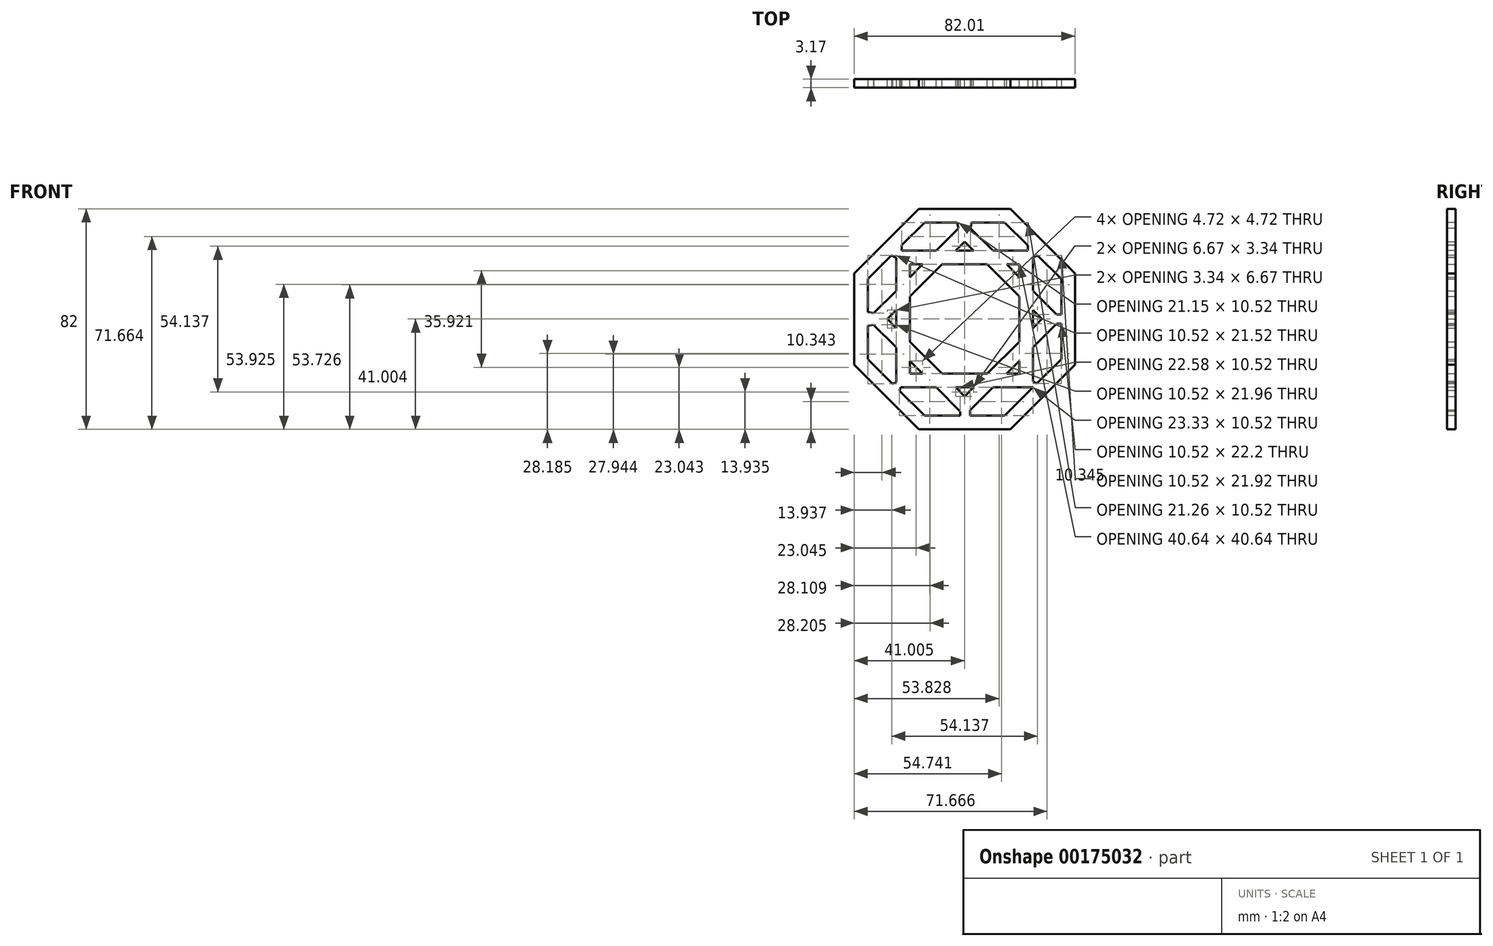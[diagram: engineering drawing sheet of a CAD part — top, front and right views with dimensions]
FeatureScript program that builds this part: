
annotation { "Feature Type Name" : "Feature", "Feature Type Description" : "" }
export const myFeature = defineFeature(function(context is Context, id is Id, definition is map)
    precondition{}
    {
        {
            var Q0;
            Q0=qCreatedBy(makeId("Front.planeOp"),FACE);
            var sketch = newSketch(context, id + "F0", { "sketchPlane" : qUnion([Q0])});
            skLineSegment(sketch, "E0.bottom", {"start": v(2.39, 24.41) * mm, "end": v(53.19, 24.41) * mm});
            skLineSegment(sketch, "E0.top", {"start": v(2.39, -26.39) * mm, "end": v(53.19, -26.39) * mm});
            skLineSegment(sketch, "E0.left", {"start": v(2.39, 24.41) * mm, "end": v(2.39, -26.39) * mm});
            skLineSegment(sketch, "E0.right", {"start": v(53.19, 24.41) * mm, "end": v(53.19, -26.39) * mm});
            skLineSegment(sketch, "E1.bottom", {"start": v(7.47, 19.33) * mm, "end": v(48.1, 19.33) * mm});
            skLineSegment(sketch, "E1.top", {"start": v(7.47, -21.3) * mm, "end": v(48.1, -21.3) * mm});
            skLineSegment(sketch, "E1.left", {"start": v(7.47, 19.33) * mm, "end": v(7.47, -21.3) * mm});
            skLineSegment(sketch, "E1.right", {"start": v(48.1, 19.33) * mm, "end": v(48.1, -21.3) * mm});
            skLineSegment(sketch, "E2.0", {"start": v(63.7, -0.99) * mm, "end": v(27.79, -36.9) * mm});
            skLineSegment(sketch, "E2.1", {"start": v(27.79, -36.9) * mm, "end": v(-8.14, -0.99) * mm});
            skLineSegment(sketch, "E2.2", {"start": v(-8.14, -0.99) * mm, "end": v(27.79, 34.93) * mm});
            skLineSegment(sketch, "E2.3", {"start": v(27.79, 34.93) * mm, "end": v(63.7, -0.99) * mm});
            skPoint(sketch, "E2.0.midPoint", {"position": v(45.75, -18.95) * mm});
            skPoint(sketch, "E3.0.midPoint", {"position": v(2.39, -0.99) * mm});
            skLineSegment(sketch, "E4.0", {"start": v(56.52, -0.99) * mm, "end": v(27.79, -29.72) * mm});
            skLineSegment(sketch, "E4.1", {"start": v(27.79, -29.72) * mm, "end": v(-0.95, -0.99) * mm});
            skLineSegment(sketch, "E4.2", {"start": v(-0.95, -0.99) * mm, "end": v(27.79, 27.75) * mm});
            skLineSegment(sketch, "E4.3", {"start": v(27.79, 27.75) * mm, "end": v(56.52, -0.99) * mm});
            skPoint(sketch, "E4.0.midPoint", {"position": v(42.15, -15.35) * mm});
            skPoint(sketch, "E5", {"position": v(48.1, -0.99) * mm});
            skPoint(sketch, "E6", {"position": v(27.79, 24.41) * mm});
            skPoint(sketch, "E7", {"position": v(53.19, -0.99) * mm});
            skCircle(sketch, "E8.cCircle", {"center": v(27.79, -0.99) * mm, "radius": 41 * mm, "construction": true});
            skLineSegment(sketch, "E8.0", {"start": v(-13.22, 16) * mm, "end": v(10.8, 40.01) * mm});
            skLineSegment(sketch, "E8.1", {"start": v(10.8, 40.01) * mm, "end": v(44.77, 40.01) * mm});
            skLineSegment(sketch, "E8.2", {"start": v(44.77, 40.01) * mm, "end": v(68.79, 16) * mm});
            skLineSegment(sketch, "E8.3", {"start": v(68.79, 16) * mm, "end": v(68.79, -17.97) * mm});
            skLineSegment(sketch, "E8.4", {"start": v(68.79, -17.97) * mm, "end": v(44.77, -41.99) * mm});
            skLineSegment(sketch, "E8.5", {"start": v(44.77, -41.99) * mm, "end": v(10.8, -41.99) * mm});
            skLineSegment(sketch, "E8.6", {"start": v(10.8, -41.99) * mm, "end": v(-13.22, -17.97) * mm});
            skLineSegment(sketch, "E8.7", {"start": v(-13.22, -17.97) * mm, "end": v(-13.22, 16) * mm});
            skPoint(sketch, "E8.0.midPoint", {"position": v(-1.2, 28) * mm});
            skPoint(sketch, "E9", {"position": v(-13.22, -0.99) * mm});
            skPoint(sketch, "E10", {"position": v(68.79, -0.99) * mm});
            skPoint(sketch, "E11", {"position": v(27.79, 40.01) * mm});
            skPoint(sketch, "E12", {"position": v(27.79, -41.99) * mm});
            skCircle(sketch, "E13.cCircle", {"center": v(27.79, -0.99) * mm, "radius": 35.92 * mm, "construction": true});
            skLineSegment(sketch, "E13.0", {"start": v(12.9, 34.93) * mm, "end": v(42.66, 34.93) * mm});
            skLineSegment(sketch, "E13.1", {"start": v(42.66, 34.93) * mm, "end": v(63.7, 13.9) * mm});
            skLineSegment(sketch, "E13.2", {"start": v(63.7, 13.9) * mm, "end": v(63.7, -15.87) * mm});
            skLineSegment(sketch, "E13.3", {"start": v(63.7, -15.87) * mm, "end": v(42.66, -36.9) * mm});
            skLineSegment(sketch, "E13.4", {"start": v(42.66, -36.9) * mm, "end": v(12.9, -36.9) * mm});
            skLineSegment(sketch, "E13.5", {"start": v(12.9, -36.9) * mm, "end": v(-8.14, -15.87) * mm});
            skLineSegment(sketch, "E13.6", {"start": v(-8.14, -15.87) * mm, "end": v(-8.14, 13.9) * mm});
            skLineSegment(sketch, "E13.7", {"start": v(-8.14, 13.9) * mm, "end": v(12.9, 34.93) * mm});
            skPoint(sketch, "E13.0.midPoint", {"position": v(27.79, 34.93) * mm});
            skSolve(sketch);
        }
        {
            var Q0;
            Q0 = qSketchRegion(id + "F0", true);
            var Q1;
            {var subQ1=sQuery(id+"F0.wireOp",EDGE,"E2.2");var subQ3=sQuery(id+"F0.wireOp",EDGE,"E0.bottom");var subQ7=makeQuery(id+"F0.imprint","INTERSECT",VERTEX,{"derivedFrom":[subQ3,subQ1]});Q1=makeQuery(id+"F0.imprint","IMPRINT",FACE,{"disambiguationData":[TD([[makeQuery(id+"F0.imprint","IMPRINT",EDGE,{"disambiguationData":[TD([[subQ7,-1.0]])],"derivedFrom":subQ3}),1.0]])]});}
            var Q2;
            {var subQ0=sQuery(id+"F0.wireOp",EDGE,"E1.right");var subQ1=sQuery(id+"F0.wireOp",EDGE,"E1.bottom");var subQ2=makeQuery(id+"F0.imprint","INTERSECT",VERTEX,{"derivedFrom":[subQ1,subQ0]});Q2=makeQuery(id+"F0.imprint","IMPRINT",FACE,{"disambiguationData":[TD([[makeQuery(id+"F0.imprint","IMPRINT",EDGE,{"disambiguationData":[TD([[subQ2,1.0]])],"derivedFrom":subQ1}),1.0]])]});}
            var Q3;
            {var subQ0=sQuery(id+"F0.wireOp",EDGE,"E2.3");var subQ3=sQuery(id+"F0.wireOp",EDGE,"E0.right");var subQ4=makeQuery(id+"F0.imprint","INTERSECT",VERTEX,{"derivedFrom":[subQ3,subQ0]});Q3=makeQuery(id+"F0.imprint","IMPRINT",FACE,{"disambiguationData":[TD([[makeQuery(id+"F0.imprint","IMPRINT",EDGE,{"disambiguationData":[TD([[subQ4,-1.0]])],"derivedFrom":subQ3}),1.0]])]});}
            var Q4;
            {var subQ0=sQuery(id+"F0.wireOp",EDGE,"E1.right");var subQ1=sQuery(id+"F0.wireOp",EDGE,"E1.top");var subQ2=makeQuery(id+"F0.imprint","INTERSECT",VERTEX,{"derivedFrom":[subQ1,subQ0]});Q4=makeQuery(id+"F0.imprint","IMPRINT",FACE,{"disambiguationData":[TD([[makeQuery(id+"F0.imprint","IMPRINT",EDGE,{"disambiguationData":[TD([[subQ2,1.0]])],"derivedFrom":subQ1}),-1.0]])]});}
            var Q5;
            {var subQ0=sQuery(id+"F0.wireOp",EDGE,"E2.1");var subQ3=sQuery(id+"F0.wireOp",EDGE,"E0.top");var subQ4=makeQuery(id+"F0.imprint","INTERSECT",VERTEX,{"derivedFrom":[subQ3,subQ0]});Q5=makeQuery(id+"F0.imprint","IMPRINT",FACE,{"disambiguationData":[TD([[makeQuery(id+"F0.imprint","IMPRINT",EDGE,{"disambiguationData":[TD([[subQ4,-1.0]])],"derivedFrom":subQ3}),-1.0]])]});}
            var Q6;
            {var subQ0=sQuery(id+"F0.wireOp",EDGE,"E1.left");var subQ1=sQuery(id+"F0.wireOp",EDGE,"E1.top");var subQ2=makeQuery(id+"F0.imprint","INTERSECT",VERTEX,{"derivedFrom":[subQ1,subQ0]});Q6=makeQuery(id+"F0.imprint","IMPRINT",FACE,{"disambiguationData":[TD([[makeQuery(id+"F0.imprint","IMPRINT",EDGE,{"disambiguationData":[TD([[subQ2,-1.0]])],"derivedFrom":subQ1}),-1.0]])]});}
            var Q7;
            {var subQ0=sQuery(id+"F0.wireOp",EDGE,"E2.2");var subQ3=sQuery(id+"F0.wireOp",EDGE,"E0.left");var subQ4=makeQuery(id+"F0.imprint","INTERSECT",VERTEX,{"derivedFrom":[subQ3,subQ0]});Q7=makeQuery(id+"F0.imprint","IMPRINT",FACE,{"disambiguationData":[TD([[makeQuery(id+"F0.imprint","IMPRINT",EDGE,{"disambiguationData":[TD([[subQ4,-1.0]])],"derivedFrom":subQ3}),-1.0]])]});}
            var Q8;
            {var subQ0=sQuery(id+"F0.wireOp",EDGE,"E1.left");var subQ1=sQuery(id+"F0.wireOp",EDGE,"E1.bottom");var subQ2=makeQuery(id+"F0.imprint","INTERSECT",VERTEX,{"derivedFrom":[subQ1,subQ0]});Q8=makeQuery(id+"F0.imprint","IMPRINT",FACE,{"disambiguationData":[TD([[makeQuery(id+"F0.imprint","IMPRINT",EDGE,{"disambiguationData":[TD([[subQ2,-1.0]])],"derivedFrom":subQ1}),1.0]])]});}
            var Q9;
            {var subQ0=sQuery(id+"F0.wireOp",EDGE,"E2.2");var subQ1=sQuery(id+"F0.wireOp",EDGE,"E1.bottom");var subQ2=makeQuery(id+"F0.imprint","INTERSECT",VERTEX,{"derivedFrom":[subQ1,subQ0]});Q9=makeQuery(id+"F0.imprint","IMPRINT",FACE,{"disambiguationData":[TD([[makeQuery(id+"F0.imprint","IMPRINT",EDGE,{"disambiguationData":[TD([[subQ2,-1.0]])],"derivedFrom":subQ1}),-1.0]])]});}
            var Q10;
            {var subQ0=sQuery(id+"F0.wireOp",EDGE,"E4.2");var subQ1=sQuery(id+"F0.wireOp",EDGE,"E0.bottom");var subQ2=makeQuery(id+"F0.imprint","INTERSECT",VERTEX,{"derivedFrom":[subQ1,subQ0]});Q10=makeQuery(id+"F0.imprint","IMPRINT",FACE,{"disambiguationData":[TD([[makeQuery(id+"F0.imprint","IMPRINT",EDGE,{"disambiguationData":[TD([[subQ2,-1.0]])],"derivedFrom":subQ1}),-1.0]])]});}
            var Q11;
            {var subQ0=sQuery(id+"F0.wireOp",EDGE,"E4.3");var subQ1=sQuery(id+"F0.wireOp",EDGE,"E1.bottom");var subQ2=makeQuery(id+"F0.imprint","INTERSECT",VERTEX,{"derivedFrom":[subQ1,subQ0]});Q11=makeQuery(id+"F0.imprint","IMPRINT",FACE,{"disambiguationData":[TD([[makeQuery(id+"F0.imprint","IMPRINT",EDGE,{"disambiguationData":[TD([[subQ2,-1.0]])],"derivedFrom":subQ1}),-1.0]])]});}
            var Q12;
            {var subQ0=sQuery(id+"F0.wireOp",EDGE,"E4.3");var subQ1=sQuery(id+"F0.wireOp",EDGE,"E0.right");var subQ2=makeQuery(id+"F0.imprint","INTERSECT",VERTEX,{"derivedFrom":[subQ1,subQ0]});Q12=makeQuery(id+"F0.imprint","IMPRINT",FACE,{"disambiguationData":[TD([[makeQuery(id+"F0.imprint","IMPRINT",EDGE,{"disambiguationData":[TD([[subQ2,-1.0]])],"derivedFrom":subQ1}),-1.0]])]});}
            var Q13;
            {var subQ0=sQuery(id+"F0.wireOp",EDGE,"E4.0");var subQ1=sQuery(id+"F0.wireOp",EDGE,"E1.top");var subQ2=makeQuery(id+"F0.imprint","INTERSECT",VERTEX,{"derivedFrom":[subQ1,subQ0]});Q13=makeQuery(id+"F0.imprint","IMPRINT",FACE,{"disambiguationData":[TD([[makeQuery(id+"F0.imprint","IMPRINT",EDGE,{"disambiguationData":[TD([[subQ2,-1.0]])],"derivedFrom":subQ1}),1.0]])]});}
            var Q14;
            {var subQ0=sQuery(id+"F0.wireOp",EDGE,"E4.1");var subQ1=sQuery(id+"F0.wireOp",EDGE,"E0.top");var subQ2=makeQuery(id+"F0.imprint","INTERSECT",VERTEX,{"derivedFrom":[subQ1,subQ0]});Q14=makeQuery(id+"F0.imprint","IMPRINT",FACE,{"disambiguationData":[TD([[makeQuery(id+"F0.imprint","IMPRINT",EDGE,{"disambiguationData":[TD([[subQ2,-1.0]])],"derivedFrom":subQ1}),1.0]])]});}
            var Q15;
            {var subQ0=sQuery(id+"F0.wireOp",EDGE,"E2.1");var subQ1=sQuery(id+"F0.wireOp",EDGE,"E1.top");var subQ2=makeQuery(id+"F0.imprint","INTERSECT",VERTEX,{"derivedFrom":[subQ1,subQ0]});Q15=makeQuery(id+"F0.imprint","IMPRINT",FACE,{"disambiguationData":[TD([[makeQuery(id+"F0.imprint","IMPRINT",EDGE,{"disambiguationData":[TD([[subQ2,-1.0]])],"derivedFrom":subQ1}),1.0]])]});}
            var Q16;
            {var subQ0=sQuery(id+"F0.wireOp",EDGE,"E4.2");var subQ1=sQuery(id+"F0.wireOp",EDGE,"E0.left");var subQ2=makeQuery(id+"F0.imprint","INTERSECT",VERTEX,{"derivedFrom":[subQ1,subQ0]});Q16=makeQuery(id+"F0.imprint","IMPRINT",FACE,{"disambiguationData":[TD([[makeQuery(id+"F0.imprint","IMPRINT",EDGE,{"disambiguationData":[TD([[subQ2,-1.0]])],"derivedFrom":subQ1}),1.0]])]});}
            var Q17;
            {var subQ0=sQuery(id+"F0.wireOp",EDGE,"E2.2");var subQ1=sQuery(id+"F0.wireOp",EDGE,"E0.bottom");var subQ2=makeQuery(id+"F0.imprint","INTERSECT",VERTEX,{"derivedFrom":[subQ1,subQ0]});Q17=makeQuery(id+"F0.imprint","IMPRINT",FACE,{"disambiguationData":[TD([[makeQuery(id+"F0.imprint","IMPRINT",EDGE,{"disambiguationData":[TD([[subQ2,-1.0]])],"derivedFrom":subQ1}),-1.0]])]});}
            var Q18;
            {var subQ0=sQuery(id+"F0.wireOp",EDGE,"E4.3");var subQ1=sQuery(id+"F0.wireOp",EDGE,"E0.bottom");var subQ2=makeQuery(id+"F0.imprint","INTERSECT",VERTEX,{"derivedFrom":[subQ1,subQ0]});Q18=makeQuery(id+"F0.imprint","IMPRINT",FACE,{"disambiguationData":[TD([[makeQuery(id+"F0.imprint","IMPRINT",EDGE,{"disambiguationData":[TD([[subQ2,-1.0]])],"derivedFrom":subQ1}),-1.0]])]});}
            var Q19;
            {var subQ0=sQuery(id+"F0.wireOp",EDGE,"E2.3");var subQ1=sQuery(id+"F0.wireOp",EDGE,"E0.right");var subQ2=makeQuery(id+"F0.imprint","INTERSECT",VERTEX,{"derivedFrom":[subQ1,subQ0]});Q19=makeQuery(id+"F0.imprint","IMPRINT",FACE,{"disambiguationData":[TD([[makeQuery(id+"F0.imprint","IMPRINT",EDGE,{"disambiguationData":[TD([[subQ2,-1.0]])],"derivedFrom":subQ1}),-1.0]])]});}
            var Q20;
            {var subQ0=sQuery(id+"F0.wireOp",EDGE,"E4.0");var subQ1=sQuery(id+"F0.wireOp",EDGE,"E0.right");var subQ2=makeQuery(id+"F0.imprint","INTERSECT",VERTEX,{"derivedFrom":[subQ1,subQ0]});Q20=makeQuery(id+"F0.imprint","IMPRINT",FACE,{"disambiguationData":[TD([[makeQuery(id+"F0.imprint","IMPRINT",EDGE,{"disambiguationData":[TD([[subQ2,-1.0]])],"derivedFrom":subQ1}),-1.0]])]});}
            var Q21;
            {var subQ0=sQuery(id+"F0.wireOp",EDGE,"E4.0");var subQ1=sQuery(id+"F0.wireOp",EDGE,"E0.top");var subQ2=makeQuery(id+"F0.imprint","INTERSECT",VERTEX,{"derivedFrom":[subQ1,subQ0]});Q21=makeQuery(id+"F0.imprint","IMPRINT",FACE,{"disambiguationData":[TD([[makeQuery(id+"F0.imprint","IMPRINT",EDGE,{"disambiguationData":[TD([[subQ2,-1.0]])],"derivedFrom":subQ1}),1.0]])]});}
            var Q22;
            {var subQ0=sQuery(id+"F0.wireOp",EDGE,"E2.1");var subQ1=sQuery(id+"F0.wireOp",EDGE,"E0.top");var subQ2=makeQuery(id+"F0.imprint","INTERSECT",VERTEX,{"derivedFrom":[subQ1,subQ0]});Q22=makeQuery(id+"F0.imprint","IMPRINT",FACE,{"disambiguationData":[TD([[makeQuery(id+"F0.imprint","IMPRINT",EDGE,{"disambiguationData":[TD([[subQ2,-1.0]])],"derivedFrom":subQ1}),1.0]])]});}
            var Q23;
            {var subQ0=sQuery(id+"F0.wireOp",EDGE,"E4.1");var subQ1=sQuery(id+"F0.wireOp",EDGE,"E0.left");var subQ2=makeQuery(id+"F0.imprint","INTERSECT",VERTEX,{"derivedFrom":[subQ1,subQ0]});Q23=makeQuery(id+"F0.imprint","IMPRINT",FACE,{"disambiguationData":[TD([[makeQuery(id+"F0.imprint","IMPRINT",EDGE,{"disambiguationData":[TD([[subQ2,-1.0]])],"derivedFrom":subQ1}),1.0]])]});}
            var Q24;
            {var subQ0=sQuery(id+"F0.wireOp",EDGE,"E2.2");var subQ1=sQuery(id+"F0.wireOp",EDGE,"E0.left");var subQ2=makeQuery(id+"F0.imprint","INTERSECT",VERTEX,{"derivedFrom":[subQ1,subQ0]});Q24=makeQuery(id+"F0.imprint","IMPRINT",FACE,{"disambiguationData":[TD([[makeQuery(id+"F0.imprint","IMPRINT",EDGE,{"disambiguationData":[TD([[subQ2,-1.0]])],"derivedFrom":subQ1}),1.0]])]});}
            extrude(context, id + "F1", {"entities" : qUnion([Q0, Q1, Q2, Q3, Q4, Q5, Q6, Q7, Q8, Q9, Q10, Q11, Q12, Q13, Q14, Q15, Q16, Q17, Q18, Q19, Q20, Q21, Q22, Q23, Q24]), "depth" : 3.17 * mm});
        }
        {
            var Q0;
            Q0=makeQuery(id+"F1.opExtrude","CAP_FACE",FACE,{"disambiguationData":[OSD([sQuery(id+"F0.wireOp",EDGE,"E0.bottom"),sQuery(id+"F0.wireOp",EDGE,"E0.top"),sQuery(id+"F0.wireOp",EDGE,"E0.left"),sQuery(id+"F0.wireOp",EDGE,"E0.right"),sQuery(id+"F0.wireOp",EDGE,"E1.bottom"),sQuery(id+"F0.wireOp",EDGE,"E1.top"),sQuery(id+"F0.wireOp",EDGE,"E1.left"),sQuery(id+"F0.wireOp",EDGE,"E1.right"),sQuery(id+"F0.wireOp",EDGE,"E2.0"),sQuery(id+"F0.wireOp",EDGE,"E2.1"),sQuery(id+"F0.wireOp",EDGE,"E2.2"),sQuery(id+"F0.wireOp",EDGE,"E2.3"),sQuery(id+"F0.wireOp",EDGE,"E4.0"),sQuery(id+"F0.wireOp",EDGE,"E4.1"),sQuery(id+"F0.wireOp",EDGE,"E4.2"),sQuery(id+"F0.wireOp",EDGE,"E4.3")])],"isStart":false});
            var sketch = newSketch(context, id + "F2", { "sketchPlane" : qUnion([Q0])});
            skLineSegment(sketch, "E14", {"start": v(0.67, 22.7) * mm, "end": v(2.39, 21.82) * mm});
            skLineSegment(sketch, "E15", {"start": v(2.39, 21.82) * mm, "end": v(2.39, 24.41) * mm});
            skLineSegment(sketch, "E16", {"start": v(2.39, 24.41) * mm, "end": v(0.67, 22.7) * mm});
            skLineSegment(sketch, "E17", {"start": v(2.39, 24.41) * mm, "end": v(4.4, 26.44) * mm});
            skLineSegment(sketch, "E18", {"start": v(4.4, 26.44) * mm, "end": v(4.4, 24.41) * mm});
            skLineSegment(sketch, "E19", {"start": v(4.4, 24.41) * mm, "end": v(2.39, 24.41) * mm});
            skLineSegment(sketch, "E20", {"start": v(25.04, 34.93) * mm, "end": v(25.56, 32.71) * mm});
            skLineSegment(sketch, "E21", {"start": v(25.56, 32.71) * mm, "end": v(27.79, 34.93) * mm});
            skLineSegment(sketch, "E22", {"start": v(27.79, 34.93) * mm, "end": v(25.04, 34.93) * mm});
            skLineSegment(sketch, "E23", {"start": v(27.79, 34.93) * mm, "end": v(30.38, 34.93) * mm});
            skLineSegment(sketch, "E24", {"start": v(30.38, 34.93) * mm, "end": v(29.98, 32.74) * mm});
            skLineSegment(sketch, "E25", {"start": v(29.98, 32.74) * mm, "end": v(27.79, 34.93) * mm});
            skLineSegment(sketch, "E26", {"start": v(51.24, 26.36) * mm, "end": v(51.24, 24.41) * mm});
            skLineSegment(sketch, "E27", {"start": v(51.24, 24.41) * mm, "end": v(53.19, 24.41) * mm});
            skLineSegment(sketch, "E28", {"start": v(53.19, 24.41) * mm, "end": v(51.24, 26.36) * mm});
            skLineSegment(sketch, "E29", {"start": v(53.19, 24.41) * mm, "end": v(53.19, 21.96) * mm});
            skLineSegment(sketch, "E30", {"start": v(53.19, 21.96) * mm, "end": v(54.9, 22.7) * mm});
            skLineSegment(sketch, "E31", {"start": v(54.9, 22.7) * mm, "end": v(53.19, 24.41) * mm});
            skLineSegment(sketch, "E32", {"start": v(61.94, 0.78) * mm, "end": v(63.7, 0.78) * mm});
            skLineSegment(sketch, "E33", {"start": v(63.7, 0.78) * mm, "end": v(63.7, -0.99) * mm});
            skLineSegment(sketch, "E34", {"start": v(63.7, -0.99) * mm, "end": v(61.94, 0.78) * mm});
            skLineSegment(sketch, "E35", {"start": v(63.7, -0.99) * mm, "end": v(63.7, -2.7) * mm});
            skLineSegment(sketch, "E36", {"start": v(63.7, -2.7) * mm, "end": v(61.99, -2.7) * mm});
            skLineSegment(sketch, "E37", {"start": v(61.99, -2.7) * mm, "end": v(63.7, -0.99) * mm});
            skLineSegment(sketch, "E38", {"start": v(53.19, -26.39) * mm, "end": v(53.19, -24.22) * mm});
            skLineSegment(sketch, "E39", {"start": v(53.19, -24.22) * mm, "end": v(54.67, -24.9) * mm});
            skLineSegment(sketch, "E40", {"start": v(54.67, -24.9) * mm, "end": v(53.19, -26.39) * mm});
            skLineSegment(sketch, "E41", {"start": v(51.24, -26.39) * mm, "end": v(51.68, -27.88) * mm});
            skLineSegment(sketch, "E42", {"start": v(51.68, -27.88) * mm, "end": v(53.19, -26.39) * mm});
            skLineSegment(sketch, "E43", {"start": v(27.79, -36.9) * mm, "end": v(29.86, -34.84) * mm});
            skLineSegment(sketch, "E44", {"start": v(29.86, -34.84) * mm, "end": v(29.86, -36.9) * mm});
            skLineSegment(sketch, "E45", {"start": v(29.86, -36.9) * mm, "end": v(27.79, -36.9) * mm});
            skLineSegment(sketch, "E46", {"start": v(26.18, -35.3) * mm, "end": v(26.18, -36.9) * mm});
            skLineSegment(sketch, "E47", {"start": v(26.18, -36.9) * mm, "end": v(27.79, -36.9) * mm});
            skLineSegment(sketch, "E48", {"start": v(4.01, -26.39) * mm, "end": v(3.6, -27.6) * mm});
            skLineSegment(sketch, "E49", {"start": v(3.6, -27.6) * mm, "end": v(2.39, -26.39) * mm});
            skLineSegment(sketch, "E50", {"start": v(2.39, -26.39) * mm, "end": v(4.01, -26.39) * mm});
            skLineSegment(sketch, "E51", {"start": v(2.39, -26.39) * mm, "end": v(1.02, -25.02) * mm});
            skLineSegment(sketch, "E52", {"start": v(1.02, -25.02) * mm, "end": v(2.39, -24.61) * mm});
            skLineSegment(sketch, "E53", {"start": v(2.39, -24.61) * mm, "end": v(2.39, -26.39) * mm});
            skLineSegment(sketch, "E54", {"start": v(-8.14, -3.5) * mm, "end": v(-6.05, -3.07) * mm});
            skLineSegment(sketch, "E55", {"start": v(-6.05, -3.07) * mm, "end": v(-8.14, -0.99) * mm});
            skLineSegment(sketch, "E56", {"start": v(-8.14, -0.99) * mm, "end": v(-8.14, -3.5) * mm});
            skLineSegment(sketch, "E57", {"start": v(-8.14, -0.99) * mm, "end": v(-8.14, 1.63) * mm});
            skLineSegment(sketch, "E58", {"start": v(-8.14, 1.63) * mm, "end": v(-5.97, 1.18) * mm});
            skLineSegment(sketch, "E59", {"start": v(-5.97, 1.18) * mm, "end": v(-8.14, -0.99) * mm});
            skSolve(sketch);
        }
        {
            var Q0;
            Q0 = qSketchRegion(id + "F2", true);
            var Q1;
            {var subQ0=sQuery(id+"F2.wireOp",EDGE,"E46");Q1=makeQuery(id+"F2.imprint","IMPRINT",FACE,{"disambiguationData":[TD([[makeQuery(id+"F2.imprint","IMPRINT",EDGE,{"derivedFrom":subQ0}),1.0]])]});}
            extrude(context, id + "F3", {"entities" : qUnion([Q0, Q1]), "operationType" : NewBodyOperationType.ADD, "oppositeDirection" : true, "depth" : 3.17 * mm});
        }
    });
